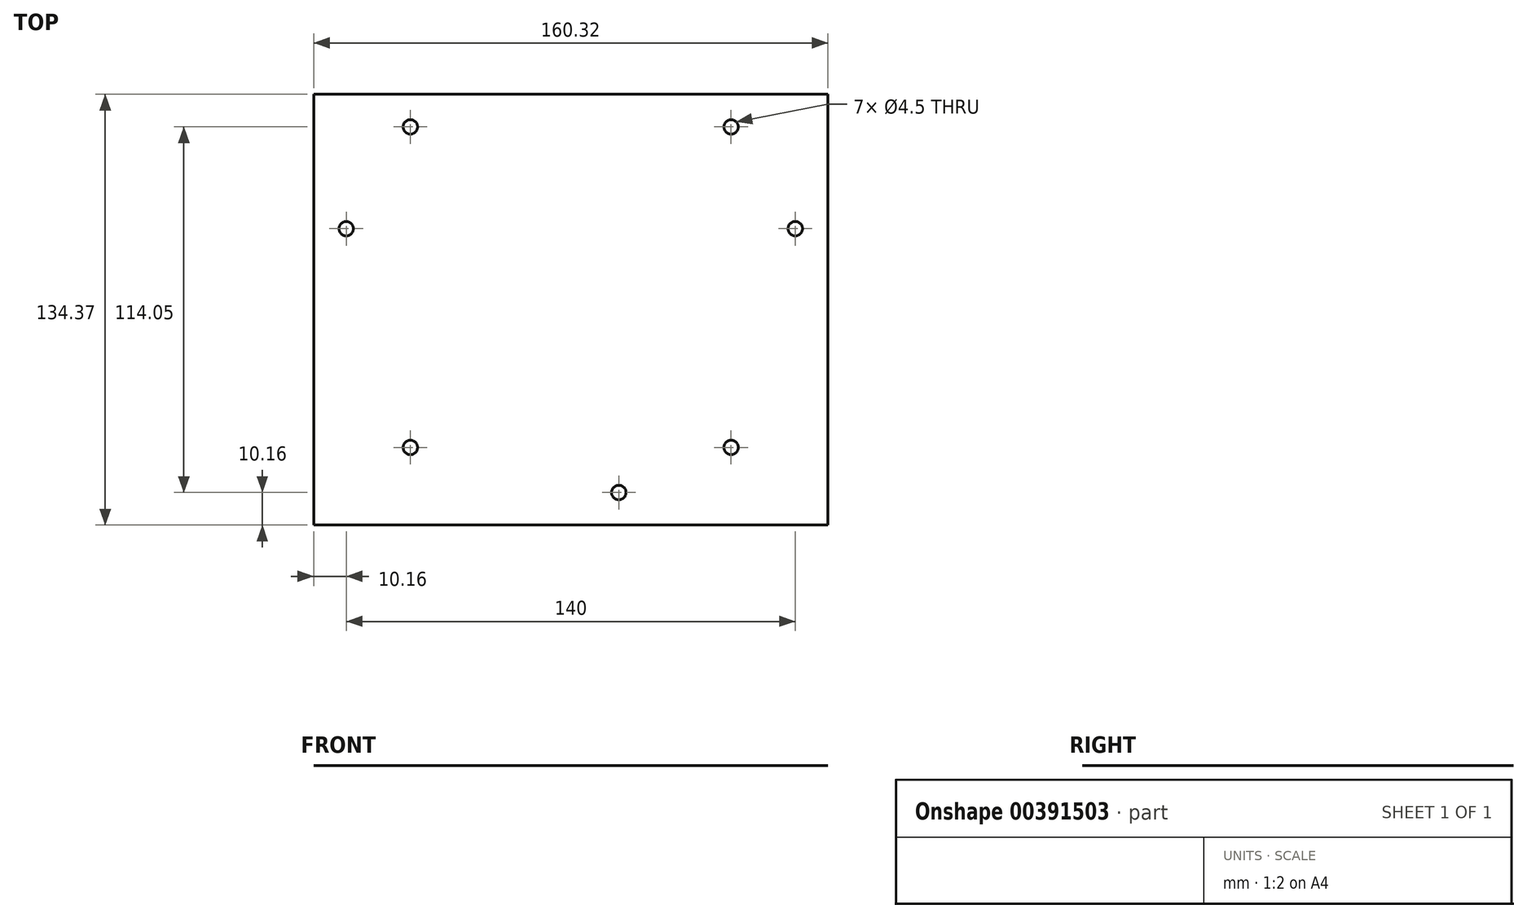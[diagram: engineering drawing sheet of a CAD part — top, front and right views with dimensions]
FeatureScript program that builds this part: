
annotation { "Feature Type Name" : "Feature", "Feature Type Description" : "" }
export const myFeature = defineFeature(function(context is Context, id is Id, definition is map)
    precondition{}
    {
        {
            var Q0;
            Q0=qCreatedBy(makeId("Top.planeOp"),FACE);
            var sketch = newSketch(context, id + "F0", { "sketchPlane" : qUnion([Q0])});
            skLineSegment(sketch, "E0.bottom", {"start": v(0, 0) * mm, "end": v(55, 0) * mm, "construction": true});
            skLineSegment(sketch, "E0.top", {"start": v(0, 82.3) * mm, "end": v(55, 82.3) * mm, "construction": true});
            skLineSegment(sketch, "E0.left", {"start": v(0, 0) * mm, "end": v(0, 82.3) * mm});
            skLineSegment(sketch, "E0.right", {"start": v(55, 0) * mm, "end": v(55, 82.3) * mm, "construction": true});
            skLineSegment(sketch, "E1.bottom", {"start": v(0, 82.3) * mm, "end": v(-85, 82.3) * mm, "construction": true});
            skLineSegment(sketch, "E1.top", {"start": v(0, 0) * mm, "end": v(-85, 0) * mm, "construction": true});
            skLineSegment(sketch, "E1.left", {"start": v(0, 82.3) * mm, "end": v(0, 0) * mm, "construction": true});
            skLineSegment(sketch, "E1.right", {"start": v(-85, 82.3) * mm, "end": v(-85, 0) * mm, "construction": true});
            skLineSegment(sketch, "E2.bottom", {"start": v(-65, 114.05) * mm, "end": v(35, 114.05) * mm, "construction": true});
            skLineSegment(sketch, "E2.top", {"start": v(-65, 14.05) * mm, "end": v(35, 14.05) * mm, "construction": true});
            skLineSegment(sketch, "E2.left", {"start": v(-65, 114.05) * mm, "end": v(-65, 14.05) * mm, "construction": true});
            skLineSegment(sketch, "E2.right", {"start": v(35, 114.05) * mm, "end": v(35, 14.05) * mm, "construction": true});
            skCircle(sketch, "E3", {"center": v(-85, 82.3) * mm, "radius": 2.25 * mm});
            skCircle(sketch, "E4", {"center": v(55, 82.3) * mm, "radius": 2.25 * mm});
            skCircle(sketch, "E5", {"center": v(0, 0) * mm, "radius": 2.25 * mm});
            skCircle(sketch, "E6", {"center": v(-65, 14.05) * mm, "radius": 2.25 * mm});
            skCircle(sketch, "E7", {"center": v(35, 14.05) * mm, "radius": 2.25 * mm});
            skCircle(sketch, "E8", {"center": v(35, 114.05) * mm, "radius": 2.25 * mm});
            skCircle(sketch, "E9", {"center": v(-65, 114.05) * mm, "radius": 2.25 * mm});
            skPoint(sketch, "E10.endSnap0", {"position": v(-65, 64.05) * mm});
            skLineSegment(sketch, "E11.bottom", {"start": v(-95.16, 124.21) * mm, "end": v(65.16, 124.21) * mm});
            skLineSegment(sketch, "E11.top", {"start": v(-95.16, -10.16) * mm, "end": v(65.16, -10.16) * mm});
            skLineSegment(sketch, "E11.left", {"start": v(-95.16, 124.2) * mm, "end": v(-95.16, -10.16) * mm});
            skLineSegment(sketch, "E11.right", {"start": v(65.16, 124.21) * mm, "end": v(65.16, -10.16) * mm});
            skLineSegment(sketch, "E12", {"start": v(-15, 124.21) * mm, "end": v(-15, 114.05) * mm, "construction": true});
            skPoint(sketch, "E12.endSnap0", {"position": v(-15, 114.05) * mm});
            skPoint(sketch, "E13.end.orphan", {"position": v(55, 41.15) * mm});
            skPoint(sketch, "E13.start.orphan", {"position": v(35, 64.05) * mm});
            skLineSegment(sketch, "E14", {"start": v(-65, 64.05) * mm, "end": v(-85, 64.05) * mm, "construction": true});
            skLineSegment(sketch, "E15", {"start": v(35, 64.05) * mm, "end": v(55, 64.05) * mm, "construction": true});
            skLineSegment(sketch, "E16", {"start": v(-15, 114.05) * mm, "end": v(-15, 82.3) * mm, "construction": true});
            skLineSegment(sketch, "E17", {"start": v(-95.16, 57.02) * mm, "end": v(-85, 57.02) * mm, "construction": true});
            skLineSegment(sketch, "E18", {"start": v(-15, -10.16) * mm, "end": v(-15, 0) * mm, "construction": true});
            skSolve(sketch);
        }
        {
            var Q0;
            Q0 = qSketchRegion(id + "F0", true);
            extrude(context, id + "F1", {"entities" : qUnion([Q0]), "depth" : 1 / 203.2 * mm});
        }
    });
